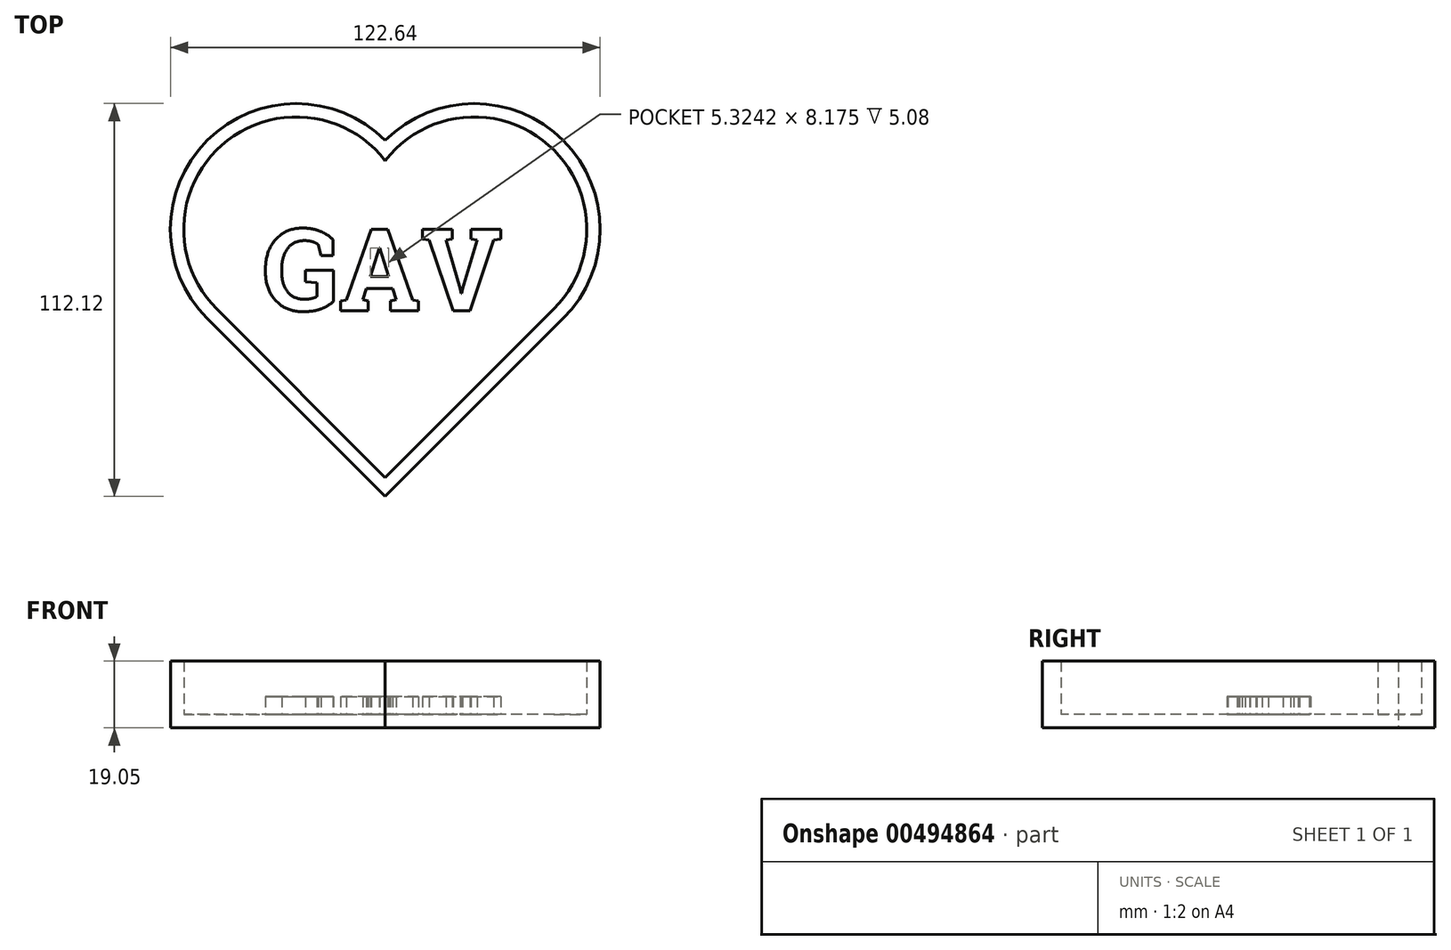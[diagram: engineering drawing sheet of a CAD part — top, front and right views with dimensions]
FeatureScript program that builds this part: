
annotation { "Feature Type Name" : "Feature", "Feature Type Description" : "" }
export const myFeature = defineFeature(function(context is Context, id is Id, definition is map)
    precondition{}
    {
        {
            var Q0;
            Q0=qCreatedBy(makeId("Top.planeOp"),FACE);
            var sketch = newSketch(context, id + "F0", { "sketchPlane" : qUnion([Q0])});
            skLineSegment(sketch, "E0", {"start": v(0, 50.8) * mm, "end": v(0, 0) * mm, "construction": true});
            skLineSegment(sketch, "E1", {"start": v(0, 0) * mm, "end": v(50.8, 0) * mm, "construction": true});
            skLineSegment(sketch, "E2", {"start": v(0, 0) * mm, "end": v(0, -50.8) * mm, "construction": true});
            skLineSegment(sketch, "E3", {"start": v(0, 0) * mm, "end": v(-50.8, 0) * mm, "construction": true});
            skLineSegment(sketch, "E4", {"start": v(-50.8, 0) * mm, "end": v(0, -50.8) * mm});
            skLineSegment(sketch, "E5", {"start": v(50.8, 0) * mm, "end": v(0, -50.8) * mm});
            skArc(sketch, "E6", {"start": v(0, 50.8) * mm, "mid": v(-50.8, 50.8) * mm, "end": v(-50.8, 0) * mm});
            skArc(sketch, "E7", {"start": v(50.8, 0) * mm, "mid": v(50.8, 50.8) * mm, "end": v(0, 50.8) * mm});
            skSolve(sketch);
        }
        {
            var Q0;
            Q0=makeQuery(id+"F0.imprint","IMPRINT",FACE,{"disambiguationData":[TD([[makeQuery(id+"F0.imprint","IMPRINT",EDGE,{"derivedFrom":sQuery(id+"F0.wireOp",EDGE,"E4")}),1.0]])]});
            extrude(context, id + "F1", {"entities" : qUnion([Q0]), "offsetDistance" : 25.4 * mm, "depth" : 19.05 * mm});
        }
        {
            var Q0;
            Q0=makeQuery(id+"F1.opExtrude","CAP_FACE",FACE,{"disambiguationData":[OSD([sQuery(id+"F0.wireOp",EDGE,"E4"),sQuery(id+"F0.wireOp",EDGE,"E5"),sQuery(id+"F0.wireOp",EDGE,"E6"),sQuery(id+"F0.wireOp",EDGE,"E7")])],"isStart":false});
            shell(context, id + "F2", {"entities" : qUnion([Q0]), "thickness" : 3.8 * mm});
        }
        {
            var Q0;
            Q0=makeQuery(id+"F2.opShell","OFFSET_FACE",FACE,{"disambiguationData":[OSD([sQuery(id+"F0.wireOp",EDGE,"E4"),sQuery(id+"F0.wireOp",EDGE,"E5"),sQuery(id+"F0.wireOp",EDGE,"E6"),sQuery(id+"F0.wireOp",EDGE,"E7")])]});
            var sketch = newSketch(context, id + "F3", { "sketchPlane" : qUnion([Q0])});
            skLineSegment(sketch, "E8.bottom", {"start": v(34.93, 25.75) * mm, "end": v(-34.93, 25.75) * mm, "construction": true});
            skLineSegment(sketch, "E8.top", {"start": v(34.93, 2.26) * mm, "end": v(-34.93, 2.26) * mm, "construction": true});
            skLineSegment(sketch, "E8.left", {"start": v(34.92, 25.75) * mm, "end": v(34.92, 2.26) * mm, "construction": true});
            skLineSegment(sketch, "E8.right", {"start": v(-34.93, 25.75) * mm, "end": v(-34.93, 2.26) * mm, "construction": true});
            skPoint(sketch, "E8.middle", {"position": v(0, 14) * mm});
            skText(sketch, "E9", { "text": "GAV", "fontName": "RobotoSlab-Bold.ttf"});
            const initialGuessF3  = {"E9": [-0.03493, 0.00226, 1, 0, 0.0235]};
            skSetInitialGuess(sketch, initialGuessF3);
            skSolve(sketch);
        }
        {
            var Q0;
            Q0=qSketchRegion(id+"F3",true);
            extrude(context, id + "F4", {"entities" : qUnion([Q0]), "operationType" : NewBodyOperationType.ADD, "depth" : 5.08 * mm, "offsetDistance" : 25.4 * mm});
        }
    });
